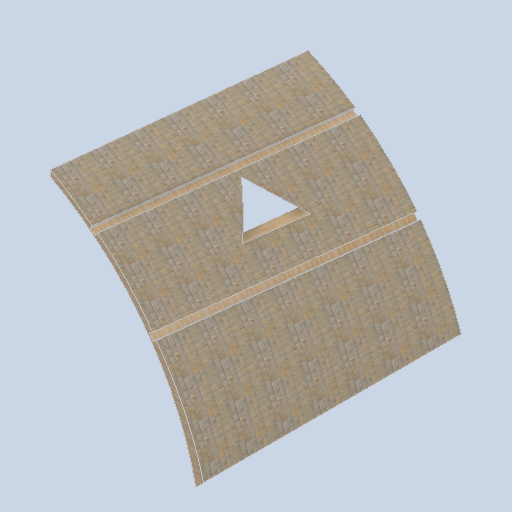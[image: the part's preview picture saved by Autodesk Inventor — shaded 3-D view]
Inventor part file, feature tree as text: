
AUTODESK INVENTOR PART (.ipt)
format: ipt  version: 2024.2 (Build 282272000, 272)  size: 354,816 bytes
history: native  units: in
note: dims shown in document units (in); Inventor stores cm internally (conversion verified against a paired STEP export)
features: other x3, sketch x3, plane x3
ambient origin geometry x8: Origin, YZ Plane, XZ Plane, XY Plane, X Axis, Y Axis, Z Axis, Center Point
bodies: Solid1 (feature_tree)
feature tree (9):
  other  "panel_block_02.ipt"
  other  "Solid1::panel_block_02.ipt"
  other  "TaggingFeature1"
  sketch  "Sketch1"  dims[d0=0.3937in]
  sketch  "Sketch2"
  sketch  "Sketch3"
  plane  "Work Plane1"
  plane  "Work Plane2"
  plane  "Work Plane3"
